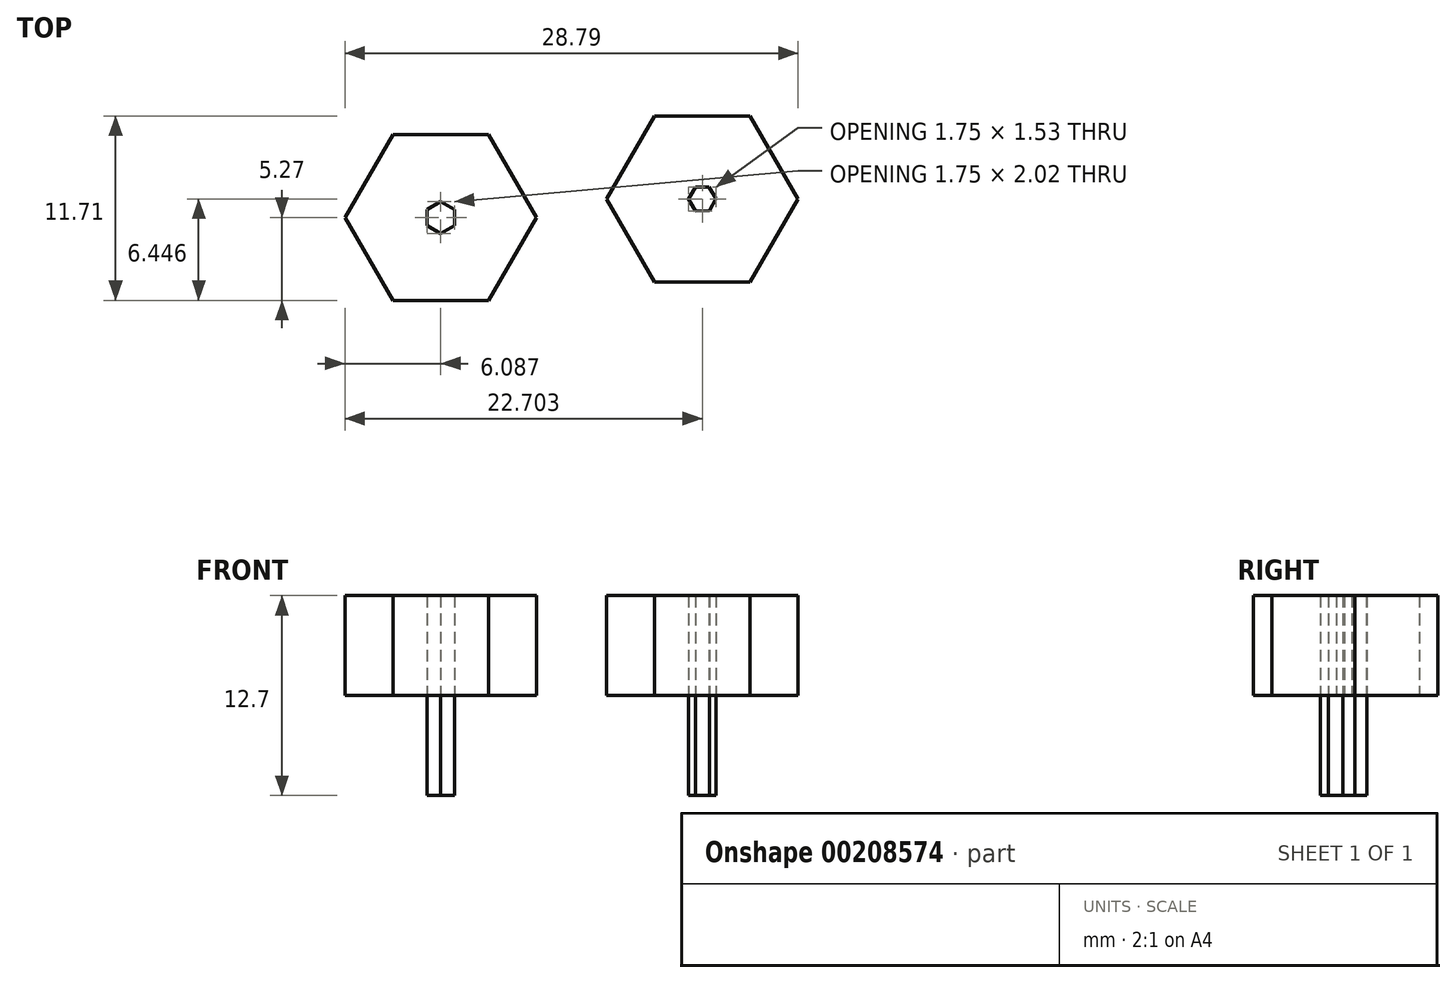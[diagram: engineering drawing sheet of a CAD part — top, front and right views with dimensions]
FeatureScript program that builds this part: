
annotation { "Feature Type Name" : "Feature", "Feature Type Description" : "" }
export const myFeature = defineFeature(function(context is Context, id is Id, definition is map)
    precondition{}
    {
        {
            var Q0;
            Q0=qCreatedBy(makeId("Top.planeOp"),FACE);
            var sketch = newSketch(context, id + "F0", { "sketchPlane" : qUnion([Q0])});
            skCircle(sketch, "E0.cCircle", {"center": v(-3.02, 0) * mm, "radius": 0.87 * mm, "construction": true});
            skLineSegment(sketch, "E0.0", {"start": v(-3.9, -0.5) * mm, "end": v(-3.9, 0.5) * mm});
            skLineSegment(sketch, "E0.1", {"start": v(-3.9, 0.5) * mm, "end": v(-3.02, 1.01) * mm});
            skLineSegment(sketch, "E0.2", {"start": v(-3.02, 1.01) * mm, "end": v(-2.15, 0.5) * mm});
            skLineSegment(sketch, "E0.3", {"start": v(-2.15, 0.5) * mm, "end": v(-2.15, -0.5) * mm});
            skLineSegment(sketch, "E0.4", {"start": v(-2.15, -0.5) * mm, "end": v(-3.02, -1.01) * mm});
            skLineSegment(sketch, "E0.5", {"start": v(-3.02, -1.01) * mm, "end": v(-3.9, -0.5) * mm});
            skPoint(sketch, "E0.0.midPoint", {"position": v(-3.9, 0) * mm});
            skCircle(sketch, "E1.cCircle", {"center": v(-3.02, 0) * mm, "radius": 5.27 * mm, "construction": true});
            skLineSegment(sketch, "E1.0", {"start": v(0.02, -5.27) * mm, "end": v(-6.06, -5.27) * mm});
            skLineSegment(sketch, "E1.1", {"start": v(-6.06, -5.27) * mm, "end": v(-9.1, 0) * mm});
            skLineSegment(sketch, "E1.2", {"start": v(-9.1, 0) * mm, "end": v(-6.06, 5.27) * mm});
            skLineSegment(sketch, "E1.3", {"start": v(-6.06, 5.27) * mm, "end": v(0.02, 5.27) * mm});
            skLineSegment(sketch, "E1.4", {"start": v(0.02, 5.27) * mm, "end": v(3.06, 0) * mm});
            skLineSegment(sketch, "E1.5", {"start": v(3.06, 0) * mm, "end": v(0.02, -5.27) * mm});
            skPoint(sketch, "E1.0.midPoint", {"position": v(-3.02, -5.27) * mm});
            skCircle(sketch, "E2.cCircle", {"center": v(13.6, 1.18) * mm, "radius": 5.27 * mm, "construction": true});
            skLineSegment(sketch, "E2.0", {"start": v(16.63, -4.1) * mm, "end": v(10.55, -4.1) * mm});
            skLineSegment(sketch, "E2.1", {"start": v(10.55, -4.1) * mm, "end": v(7.51, 1.18) * mm});
            skLineSegment(sketch, "E2.2", {"start": v(7.51, 1.18) * mm, "end": v(10.55, 6.44) * mm});
            skLineSegment(sketch, "E2.3", {"start": v(10.55, 6.44) * mm, "end": v(16.63, 6.44) * mm});
            skLineSegment(sketch, "E2.4", {"start": v(16.63, 6.44) * mm, "end": v(19.68, 1.18) * mm});
            skLineSegment(sketch, "E2.5", {"start": v(19.68, 1.18) * mm, "end": v(16.63, -4.1) * mm});
            skPoint(sketch, "E2.0.midPoint", {"position": v(13.6, -4.1) * mm});
            skCircle(sketch, "E3.cCircle", {"center": v(13.6, 1.18) * mm, "radius": 0.87 * mm, "construction": true});
            skLineSegment(sketch, "E3.0", {"start": v(13.15, 1.93) * mm, "end": v(14.02, 1.94) * mm});
            skLineSegment(sketch, "E3.1", {"start": v(14.02, 1.94) * mm, "end": v(14.47, 1.19) * mm});
            skLineSegment(sketch, "E3.2", {"start": v(14.47, 1.19) * mm, "end": v(14.04, 0.42) * mm});
            skLineSegment(sketch, "E3.3", {"start": v(14.04, 0.42) * mm, "end": v(13.17, 0.41) * mm});
            skLineSegment(sketch, "E3.4", {"start": v(13.17, 0.41) * mm, "end": v(12.72, 1.16) * mm});
            skLineSegment(sketch, "E3.5", {"start": v(12.72, 1.16) * mm, "end": v(13.15, 1.93) * mm});
            skSolve(sketch);
        }
        {
            var Q0;
            Q0=makeQuery(id+"F0.imprint","IMPRINT",FACE,{"disambiguationData":[TD([[makeQuery(id+"F0.imprint","IMPRINT",EDGE,{"derivedFrom":sQuery(id+"F0.wireOp",EDGE,"E0.0")}),1.0]])]});
            var Q1;
            Q1=makeQuery(id+"F0.imprint","IMPRINT",FACE,{"disambiguationData":[TD([[makeQuery(id+"F0.imprint","IMPRINT",EDGE,{"derivedFrom":sQuery(id+"F0.wireOp",EDGE,"E2.0")}),-1.0]])]});
            extrude(context, id + "F1", {"entities" : qUnion([Q0, Q1]), "depth" : 6.35 * mm});
        }
        {
            var Q0;
            Q0=makeQuery(id+"F0.imprint","IMPRINT",FACE,{"disambiguationData":[TD([[makeQuery(id+"F0.imprint","IMPRINT",EDGE,{"derivedFrom":sQuery(id+"F0.wireOp",EDGE,"E3.0")}),-1.0]])]});
            var Q1;
            Q1=makeQuery(id+"F0.imprint","IMPRINT",FACE,{"disambiguationData":[TD([[makeQuery(id+"F0.imprint","IMPRINT",EDGE,{"derivedFrom":sQuery(id+"F0.wireOp",EDGE,"E0.0")}),-1.0]])]});
            extrude(context, id + "F2", {"entities" : qUnion([Q0, Q1]), "depth" : 6.35 * mm, "hasSecondDirection" : true, "secondDirectionOppositeDirection" : true, "secondDirectionDepth" : 6.35 * mm});
        }
    });
